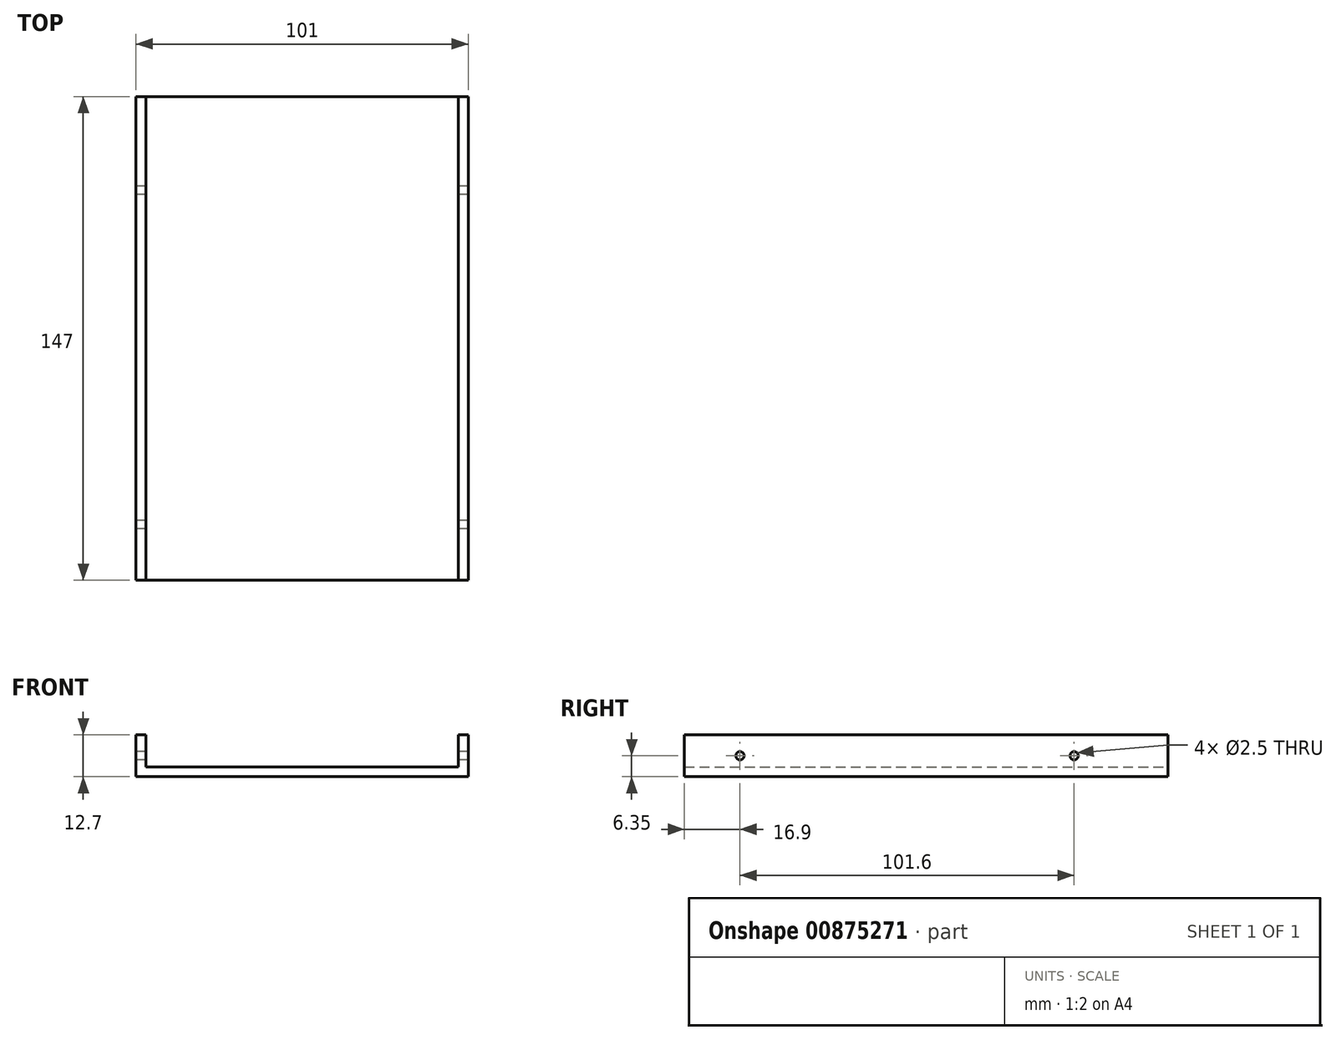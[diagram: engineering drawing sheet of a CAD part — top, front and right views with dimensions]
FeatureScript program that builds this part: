
annotation { "Feature Type Name" : "Feature", "Feature Type Description" : "" }
export const myFeature = defineFeature(function(context is Context, id is Id, definition is map)
    precondition{}
    {
        {
            assignVariable(context, id + "F0", {"variableType" : VariableType.LENGTH, "name" : "scianka", "lengthValue" : 3 * mm});
        }
        {
            var Q0;
            Q0=qCreatedBy(makeId("Top.planeOp"),FACE);
            var sketch = newSketch(context, id + "F1", { "sketchPlane" : qUnion([Q0])});
            skLineSegment(sketch, "E0.bottom", {"start": v(-50.5, 73.5) * mm, "end": v(50.5, 73.5) * mm});
            skLineSegment(sketch, "E0.top", {"start": v(-50.5, -73.5) * mm, "end": v(50.5, -73.5) * mm});
            skLineSegment(sketch, "E0.left", {"start": v(-50.5, 73.5) * mm, "end": v(-50.5, -73.5) * mm});
            skLineSegment(sketch, "E0.right", {"start": v(50.5, 73.5) * mm, "end": v(50.5, -73.5) * mm});
            skPoint(sketch, "E0.middle", {"position": v(0, 0) * mm});
            skLineSegment(sketch, "E1", {"start": v(-47.5, 73.5) * mm, "end": v(-47.5, -73.5) * mm});
            skLineSegment(sketch, "E2", {"start": v(47.5, 73.5) * mm, "end": v(47.5, -73.5) * mm});
            skSolve(sketch);
        }
        {
            var Q0;
            Q0 = qSketchRegion(id + "F1", true);
            extrude(context, id + "F2", {"entities" : qUnion([Q0]), "depth" : getVariable(context, 'scianka'), "offsetDistance" : 25 * mm});
        }
        {
            var Q0;
            {var subQ2=sQuery(id+"F1.wireOp",EDGE,"E0.left");Q0=makeQuery(id+"F1.imprint","IMPRINT",FACE,{"disambiguationData":[TD([[makeQuery(id+"F1.imprint","IMPRINT",EDGE,{"derivedFrom":subQ2}),1.0]])]});}
            var Q1;
            {var subQ0=sQuery(id+"F1.wireOp",EDGE,"E0.right");Q1=makeQuery(id+"F1.imprint","IMPRINT",FACE,{"disambiguationData":[TD([[makeQuery(id+"F1.imprint","IMPRINT",EDGE,{"derivedFrom":subQ0}),-1.0]])]});}
            extrude(context, id + "F3", {"entities" : qUnion([Q0, Q1]), "operationType" : NewBodyOperationType.ADD, "depth" : (6.35 * 2) * mm, "offsetDistance" : 25 * mm});
        }
        {
            var Q0;
            {var subQ0=sQuery(id+"F1.wireOp",EDGE,"E0.left");Q0=makeQuery(id+"F3.boolean.opBoolean","MERGE",FACE,{"derivedFrom":[makeQuery(id+"F2.opExtrude","SWEPT_FACE",FACE,{"disambiguationData":[OSD([subQ0])]}),makeQuery(id+"F3.opExtrude","SWEPT_FACE",FACE,{"disambiguationData":[OSD([subQ0])]})]});}
            var sketch = newSketch(context, id + "F4", { "sketchPlane" : qUnion([Q0])});
            skLineSegment(sketch, "E3", {"start": v(-73.5, 6.35) * mm, "end": v(73.5, 6.35) * mm, "construction": true});
            skCircle(sketch, "E4", {"center": v(-45, 6.35) * mm, "radius": 1.25 * mm});
            skCircle(sketch, "E5", {"center": v(56.6, 6.35) * mm, "radius": 1.25 * mm});
            skSolve(sketch);
        }
        {
            var Q0;
            Q0=makeQuery(id+"F4.imprint","IMPRINT",FACE,{"disambiguationData":[TD([[makeQuery(id+"F4.imprint","IMPRINT",EDGE,{"derivedFrom":sQuery(id+"F4.wireOp",EDGE,"E4")}),1.0]])]});
            var Q1;
            Q1=makeQuery(id+"F4.imprint","IMPRINT",FACE,{"disambiguationData":[TD([[makeQuery(id+"F4.imprint","IMPRINT",EDGE,{"derivedFrom":sQuery(id+"F4.wireOp",EDGE,"E5")}),1.0]])]});
            var Q2;
            Q2=sQuery(id+"F4.wireOp",EDGE,"E4");
            var Q3;
            Q3=sQuery(id+"F4.wireOp",EDGE,"E5");
            extrude(context, id + "F5", {"entities" : qUnion([Q0, Q1]), "operationType" : NewBodyOperationType.REMOVE, "surfaceEntities" : qUnion([Q2, Q3]), "endBound" : BoundingType.THROUGH_ALL, "oppositeDirection" : true, "depth" : 25 * mm, "offsetDistance" : 25 * mm});
        }
    });
